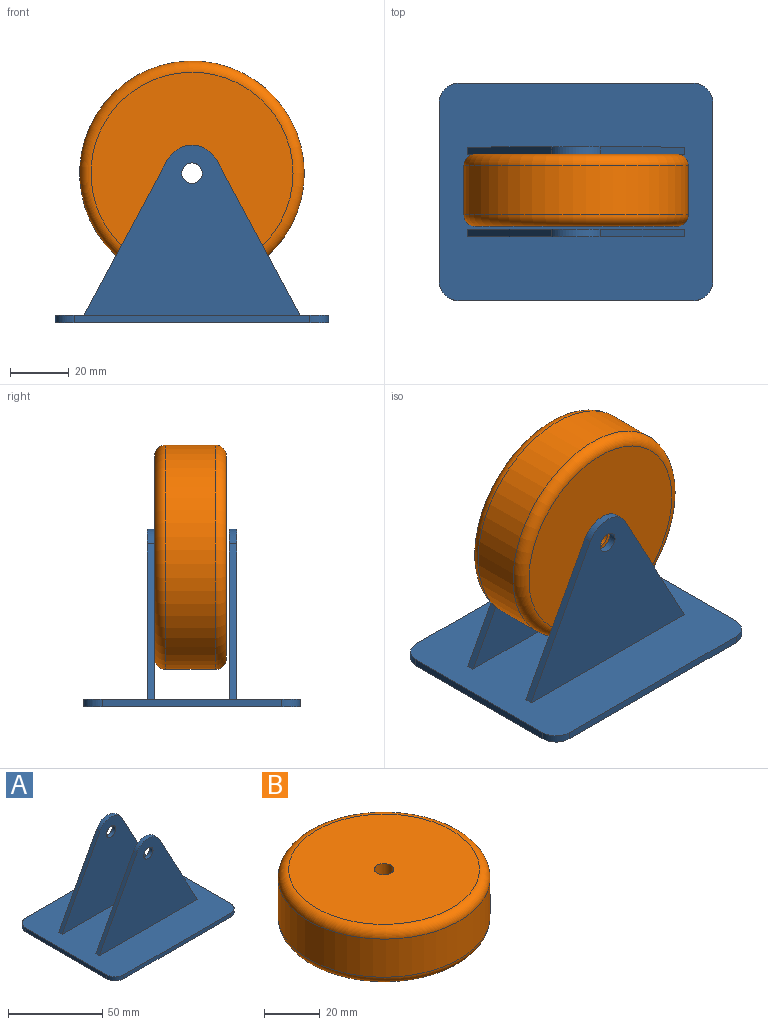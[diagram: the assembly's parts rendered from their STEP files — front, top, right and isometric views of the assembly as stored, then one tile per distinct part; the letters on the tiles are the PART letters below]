
ASSEMBLY  parts=2 mates=1
PART A: 22 faces, bbox 92.7x73.7x60.3 mm
  f0: plane 92.71x73.66mm, normal (0,0,1), area 6421.2mm2, adj f1,f2,f3,f4,f5,f6,f7,f8
  f1: plane 60.96x2.54mm, normal (1,0,0), area 154.8mm2, adj f0,f2,f8,f9
  f2: cylinder r=6.35mm len=6.35mm, axis (0,0,-1), area 25.3mm2, adj f0,f1,f3,f9
  f3: plane 80.01x2.54mm, normal (0,1,0), area 203.2mm2, adj f0,f2,f4,f9
  f4: cylinder r=6.35mm len=6.35mm, axis (0,0,-1), area 25.3mm2, adj f0,f3,f5,f9
  f5: plane 60.96x2.54mm, normal (-1,0,0), area 154.8mm2, adj f0,f4,f6,f9
  f6: cylinder r=6.35mm len=6.35mm, axis (0,0,-1), area 25.3mm2, adj f0,f5,f7,f9
  f7: plane 80.01x2.54mm, normal (0,-1,0), area 203.2mm2, adj f0,f6,f8,f9
  f8: cylinder r=6.35mm len=6.35mm, axis (0,0,-1), area 25.3mm2, adj f0,f1,f7,f9
  f9: plane 92.71x73.66mm, normal (0,0,-1), area 6794.4mm2, adj f1,f2,f3,f4,f5,f6,f7,f8
  f10: plane 52.77x28.34mm, normal (-0.88,0,0.47), area 152.1mm2, adj f0,f12,f14,f15
  f11: plane 52.77x28.34mm, normal (0.88,0,0.47), area 152.1mm2, adj f0,f12,f14,f15
  f12: cylinder r=9.53mm len=16.78mm, axis (0,1,0), area 52.2mm2, adj f10,f11,f14,f15
  f13: cylinder r=3.5mm len=7mm, axis (0,1,0), area 55.9mm2, adj f14,f15
  f14: plane 73.47x57.79mm, normal (0,-1,0), area 2402.7mm2, adj f0,f10,f11,f12,f13
  f15: plane 73.47x57.79mm, normal (0,1,0), area 2402.7mm2, adj f0,f10,f11,f12,f13
  f16: plane 52.77x28.34mm, normal (-0.88,0,0.47), area 152.1mm2, adj f0,f18,f20,f21
  f17: plane 52.77x28.34mm, normal (0.88,0,0.47), area 152.1mm2, adj f0,f18,f20,f21
  f18: cylinder r=9.53mm len=16.78mm, axis (0,-1,0), area 52.2mm2, adj f16,f17,f20,f21
  f19: cylinder r=3.5mm len=7mm, axis (0,-1,0), area 55.9mm2, adj f20,f21
  f20: plane 73.47x57.79mm, normal (0,1,0), area 2402.7mm2, adj f0,f16,f17,f18,f19
  f21: plane 73.47x57.79mm, normal (0,-1,0), area 2402.7mm2, adj f0,f16,f17,f18,f19
PART B: 6 faces, bbox 82.5x82.5x24.4 mm
  f0: cylinder r=3.5mm len=24.38mm, axis (0,0,-1), area 536.2mm2, adj f2,f3
  f1: cylinder r=38.1mm len=76.2mm, axis (0,0,-1), area 4013.1mm2, adj f4,f5
  f2: plane 68.58x68.58mm, normal (0,0,1), area 3655.4mm2, adj f0,f5
  f3: plane 68.58x68.58mm, normal (0,0,-1), area 3655.4mm2, adj f0,f4
  f4: torus R=34.29mm, axis (0,0,1), area 1380.6mm2, adj f1,f3
  f5: torus R=34.29mm, axis (0,0,1), area 1380.6mm2, adj f1,f2
PLACE A t=(0.57,0.35,-30.13)mm
PLACE B rot(axis=(-1,0,0),90deg) t=(0.57,0.86,20.67)mm
MATE revolute B.f0 <-> A.f13  axis (0,1,0) through (0.57,13.05,20.67)mm
